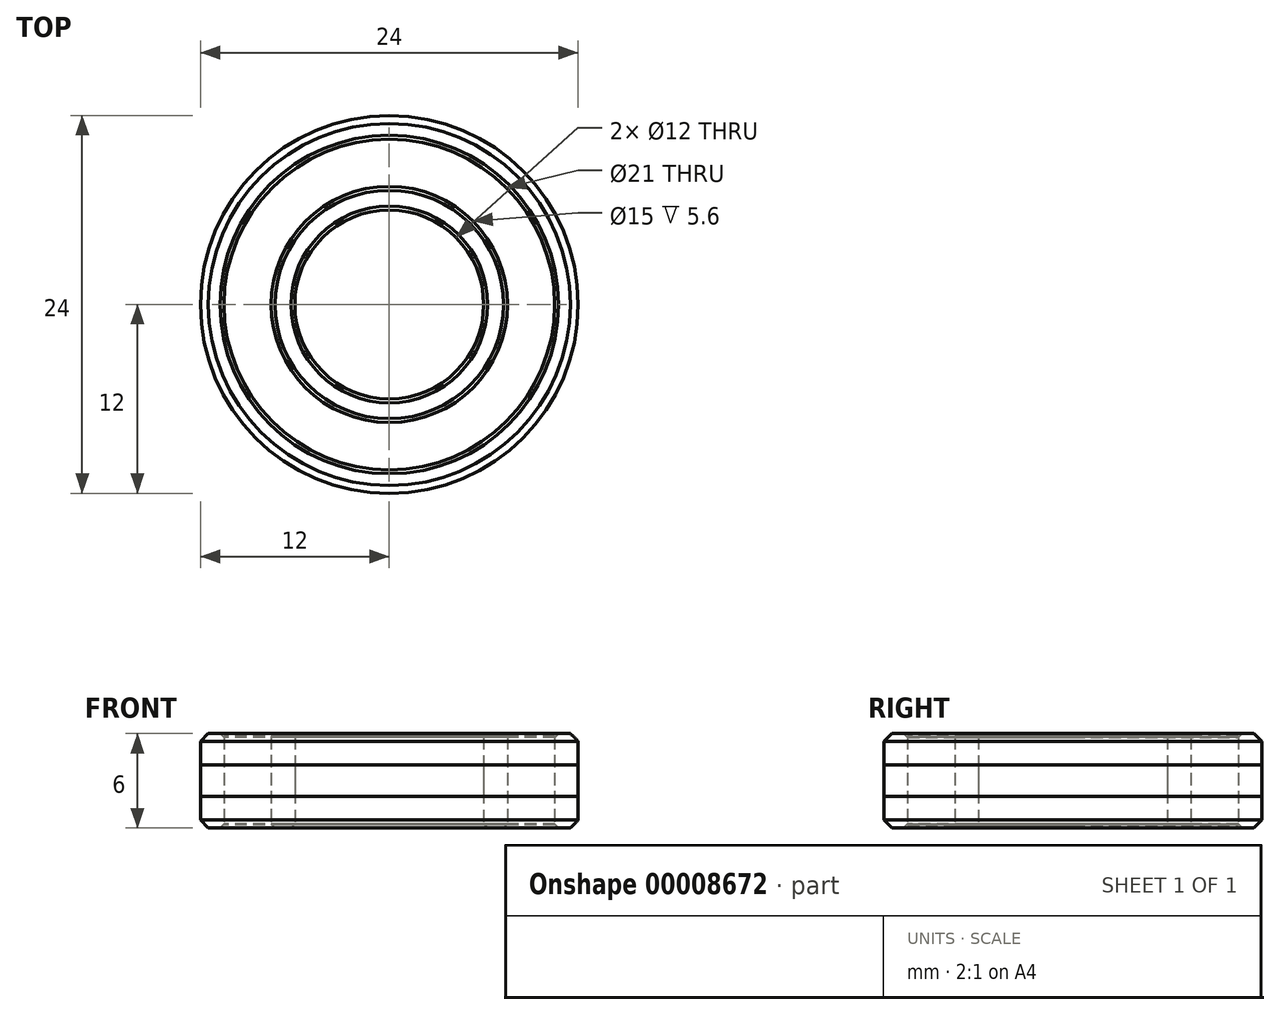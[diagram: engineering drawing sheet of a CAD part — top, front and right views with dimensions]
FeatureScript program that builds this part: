
annotation { "Feature Type Name" : "Feature", "Feature Type Description" : "" }
export const myFeature = defineFeature(function(context is Context, id is Id, definition is map)
    precondition{}
    {
        {
            var Q0;
            Q0=qCreatedBy(makeId("Top.planeOp"),FACE);
            var sketch = newSketch(context, id + "F0", { "sketchPlane" : qUnion([Q0])});
            skCircle(sketch, "E0", {"center": v(0, 0) * mm, "radius": 6 * mm});
            skCircle(sketch, "E1", {"center": v(0, 0) * mm, "radius": 7.5 * mm});
            skCircle(sketch, "E2", {"center": v(0, 0) * mm, "radius": 10.5 * mm});
            skCircle(sketch, "E3", {"center": v(0, 0) * mm, "radius": 12 * mm});
            skLineSegment(sketch, "E4", {"start": v(0, 0) * mm, "end": v(0, -12) * mm});
            skSolve(sketch);
        }
        {
            var Q0;
            Q0=makeQuery(id+"F0.imprint","IMPRINT",FACE,{"disambiguationData":[TD([[makeQuery(id+"F0.imprint","IMPRINT",EDGE,{"derivedFrom":sQuery(id+"F0.wireOp",EDGE,"E0")}),-1.0]])]});
            var Q1;
            Q1=makeQuery(id+"F0.imprint","IMPRINT",FACE,{"disambiguationData":[TD([[makeQuery(id+"F0.imprint","IMPRINT",EDGE,{"derivedFrom":sQuery(id+"F0.wireOp",EDGE,"E2")}),-1.0]])]});
            extrude(context, id + "F1", {"entities" : qUnion([Q0, Q1]), "depth" : 6 * mm, "symmetric" : true});
        }
        {
            var Q0;
            Q0=makeQuery(id+"F0.imprint","IMPRINT",FACE,{"disambiguationData":[TD([[makeQuery(id+"F0.imprint","IMPRINT",EDGE,{"derivedFrom":sQuery(id+"F0.wireOp",EDGE,"E1")}),-1.0]])]});
            extrude(context, id + "F2", {"entities" : qUnion([Q0]), "depth" : 5.6 * mm, "symmetric" : true});
        }
        {
            var Q0;
            Q0=makeQuery(id+"F1.opExtrude","CAP_EDGE",EDGE,{"disambiguationData":[OSD([sQuery(id+"F0.wireOp",EDGE,"E3")])],"isStart":false});
            var Q1;
            Q1=makeQuery(id+"F1.opExtrude","CAP_EDGE",EDGE,{"disambiguationData":[OSD([sQuery(id+"F0.wireOp",EDGE,"E3")])],"isStart":true});
            chamfer(context, id + "F3", {"entities" : qUnion([Q0, Q1]), "width" : .5 * mm, "tangentPropagation" : true});
        }
        {
            var Q0;
            Q0=makeQuery(id+"F1.opExtrude","CAP_EDGE",EDGE,{"disambiguationData":[OSD([sQuery(id+"F0.wireOp",EDGE,"E2")])],"isStart":false});
            var Q1;
            Q1=makeQuery(id+"F1.opExtrude","CAP_EDGE",EDGE,{"disambiguationData":[OSD([sQuery(id+"F0.wireOp",EDGE,"E1")])],"isStart":false});
            var Q2;
            Q2=makeQuery(id+"F1.opExtrude","CAP_EDGE",EDGE,{"disambiguationData":[OSD([sQuery(id+"F0.wireOp",EDGE,"E0")])],"isStart":false});
            var Q3;
            Q3=makeQuery(id+"F1.opExtrude","CAP_EDGE",EDGE,{"disambiguationData":[OSD([sQuery(id+"F0.wireOp",EDGE,"E0")])],"isStart":true});
            var Q4;
            Q4=makeQuery(id+"F1.opExtrude","CAP_EDGE",EDGE,{"disambiguationData":[OSD([sQuery(id+"F0.wireOp",EDGE,"E1")])],"isStart":true});
            var Q5;
            Q5=makeQuery(id+"F1.opExtrude","CAP_EDGE",EDGE,{"disambiguationData":[OSD([sQuery(id+"F0.wireOp",EDGE,"E2")])],"isStart":true});
            chamfer(context, id + "F4", {"entities" : qUnion([Q0, Q1, Q2, Q3, Q4, Q5]), "width" : .25 * mm, "tangentPropagation" : true});
        }
        {
            var Q0;
            Q0=makeQuery(id+"F0.imprint","IMPRINT",FACE,{"disambiguationData":[TD([[makeQuery(id+"F0.imprint","IMPRINT",EDGE,{"derivedFrom":sQuery(id+"F0.wireOp",EDGE,"E2")}),-1.0]])]});
            var Q1;
            Q1=makeQuery(id+"F0.imprint","IMPRINT",FACE,{"disambiguationData":[TD([[makeQuery(id+"F0.imprint","IMPRINT",EDGE,{"derivedFrom":sQuery(id+"F0.wireOp",EDGE,"E1")}),-1.0]])]});
            var Q2;
            Q2=makeQuery(id+"F0.imprint","IMPRINT",FACE,{"disambiguationData":[TD([[makeQuery(id+"F0.imprint","IMPRINT",EDGE,{"derivedFrom":sQuery(id+"F0.wireOp",EDGE,"E0")}),-1.0]])]});
            extrude(context, id + "F5", {"entities" : qUnion([Q0, Q1, Q2]), "depth" : 2 * mm, "symmetric" : true});
        }
    });
